# Revit family: Storage-Teknion-PCL__Literatura_Bookcase-R2015
name_source: partatom
category: Furniture
revit_build: Autodesk Revit Architecture 2015 (Build: 20140323_1530(x64)
units: mm (PartAtom-declared; Revit-internal decimal feet)

## types (4) — shared parameters
Assembly Code = E2020200
Depth of Shelf Unit = 13.937 "
Manufacturer = Teknion
Manufacturer Fax = 416.661.4586
Product Documentation Link = https://d2r72yk5wmppdj.cloudfront.net
Product Line = Punt Collection
Product Page URL = https://www.teknion.com
Series = Punt Collection
Sustainability Data = http://www.teknion.com
URL = www.teknion.com
Unit Weight URL = http://www.teknion.com
Warranty = http://www.teknion.com

## per-type parameters (varying)
| type | 75 Hieght | Depth | Description | Front Feet | Has Rail Shelf 46" | Has Rail Shelf 75" | Has Shelf Rail | Height | Model | Part Number | Shelf Location | Top Shelf Thickness |
| 46" Height | 20 " | 13.976 " | Literatura Open Bookcase, 46" Height, 14" Depth | No | No | No | No | 46.142 " | PCLB4614_ | PCLB | 6.969 " | 1.078 " |
| 75" Height | 1 " | 13.976 " | Literatura Open Bookcase, 75" Height, 14" Depth | No | No | No | No | 74.685 " | PCLB7514_ | PCLB | 6.969 " | 1.037 " |
| 46" Height w/ Glider Shelf | 20 " | 22.441 " | Literatura Open w/ Glider Shelf, 46" Height, 22" Depth | Yes | Yes | No | Yes | 46.142 " | PCLO4622_ | PCLO | 11.211 " | 1.078 " |
| 75" Height w/Glider Shelf | 1 " | 22.441 " | Literatura Open w/ Glider Shelf, 75" Height, 22" Depth | Yes | No | Yes | Yes | 74.685 " | PCLO7522__ | PCLO | 11.211 " | 1.037 " |

## geometry (parser evidence)
native form markers: Sweep x4
no freeform markers — native parametric forms only
